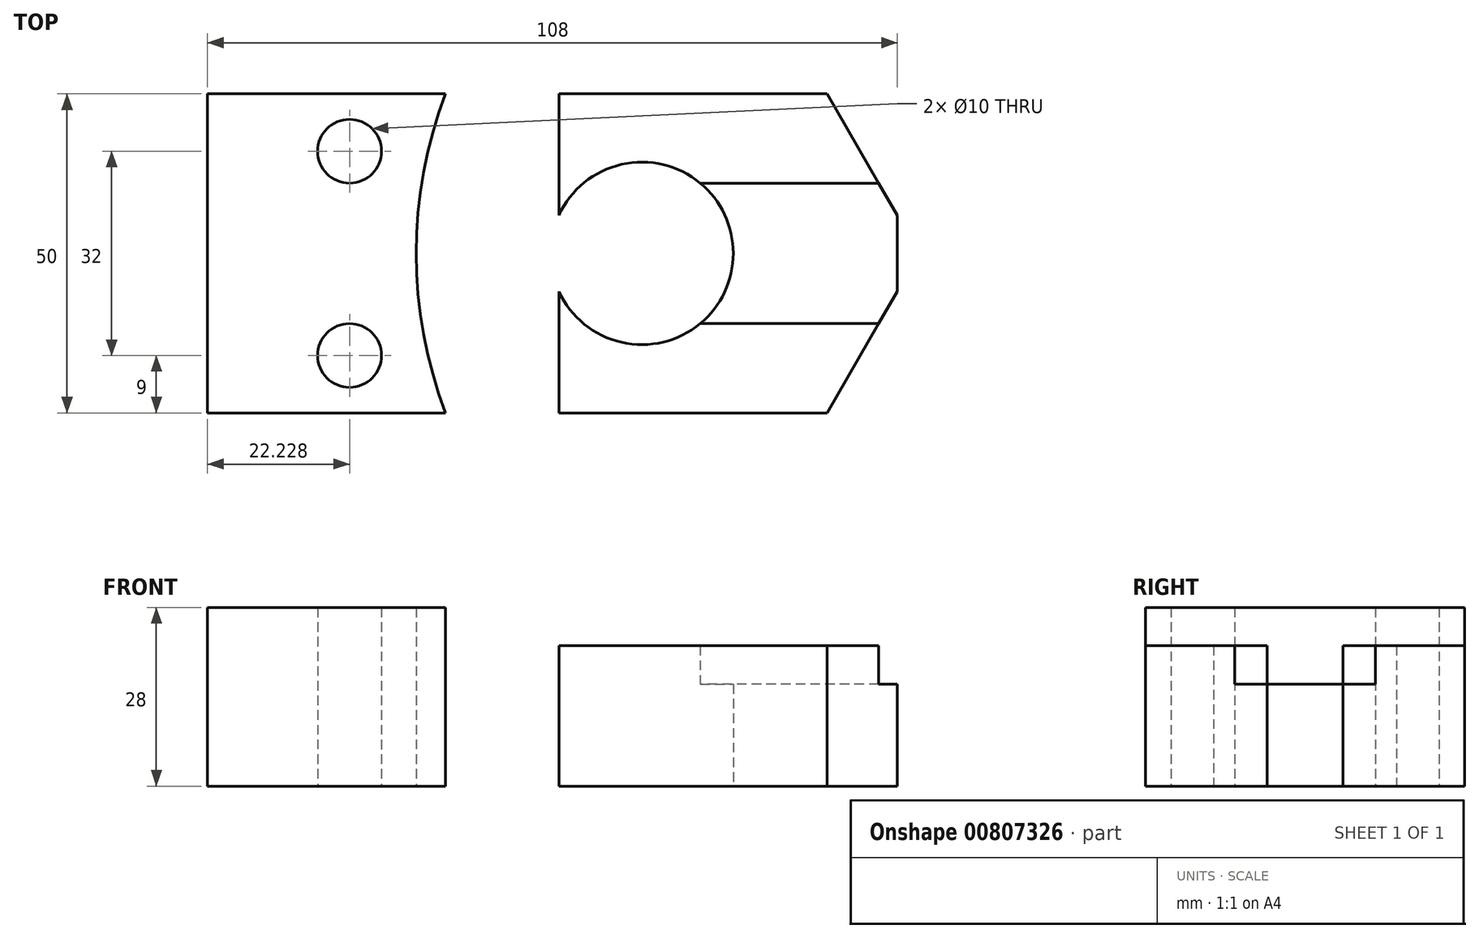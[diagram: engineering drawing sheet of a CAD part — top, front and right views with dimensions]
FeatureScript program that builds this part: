
annotation { "Feature Type Name" : "Feature", "Feature Type Description" : "" }
export const myFeature = defineFeature(function(context is Context, id is Id, definition is map)
    precondition{}
    {
        {
            var Q0;
            Q0=qCreatedBy(makeId("Top.planeOp"),FACE);
            var sketch = newSketch(context, id + "F0", { "sketchPlane" : qUnion([Q0])});
            skLineSegment(sketch, "E0", {"start": v(0, 0) * mm, "end": v(0, 50) * mm});
            skLineSegment(sketch, "E1", {"start": v(0, 50) * mm, "end": v(55, 50) * mm});
            skLineSegment(sketch, "E2", {"start": v(55, 50) * mm, "end": v(55, 0) * mm});
            skLineSegment(sketch, "E3", {"start": v(55, 0) * mm, "end": v(0, 0) * mm});
            skLineSegment(sketch, "E4", {"start": v(55, 50) * mm, "end": v(97, 50) * mm});
            skLineSegment(sketch, "E5", {"start": v(97, 50) * mm, "end": v(108, 30.95) * mm});
            skLineSegment(sketch, "E6", {"start": v(108, 30.95) * mm, "end": v(108, 19.05) * mm});
            skLineSegment(sketch, "E7", {"start": v(108, 19.05) * mm, "end": v(97, 0) * mm});
            skLineSegment(sketch, "E8", {"start": v(97, 0) * mm, "end": v(55, 0) * mm});
            skLineSegment(sketch, "E9", {"start": v(0, 25) * mm, "end": v(108, 25) * mm, "construction": true});
            skPoint(sketch, "E10", {"position": v(11, 0) * mm});
            skPoint(sketch, "E11.MirrorP", {"position": v(11, 50) * mm});
            skArc(sketch, "E12", {"start": v(11, 50) * mm, "mid": v(7.65, 25) * mm, "end": v(11, 0) * mm});
            skArc(sketch, "E13", {"start": v(37.27, 0) * mm, "mid": v(32.65, 25) * mm, "end": v(37.27, 50) * mm});
            skArc(sketch, "E14", {"start": v(24.56, 0) * mm, "mid": v(20.65, 25) * mm, "end": v(24.56, 50) * mm, "construction": true});
            skCircle(sketch, "E15", {"center": v(22.23, 41) * mm, "radius": 5 * mm});
            skCircle(sketch, "E16", {"center": v(22.23, 9) * mm, "radius": 5 * mm});
            skLineSegment(sketch, "E17", {"start": v(105.08, 14) * mm, "end": v(77.14, 14) * mm});
            skLineSegment(sketch, "E18", {"start": v(105.08, 36) * mm, "end": v(77.14, 36) * mm});
            skArc(sketch, "E19", {"start": v(77.14, 36) * mm, "mid": v(64.82, 38.94) * mm, "end": v(55, 30.96) * mm});
            skArc(sketch, "E20", {"start": v(77.14, 14) * mm, "mid": v(82.3, 25) * mm, "end": v(77.14, 36) * mm});
            skArc(sketch, "E21", {"start": v(55, 19.04) * mm, "mid": v(64.82, 11.06) * mm, "end": v(77.14, 14) * mm});
            skArc(sketch, "E22", {"start": v(55, 30.96) * mm, "mid": v(53.7, 25) * mm, "end": v(55, 19.04) * mm});
            skSolve(sketch);
        }
        {
            var Q0;
            {var subQ1=sQuery(id+"F0.wireOp",EDGE,"E12");Q0=makeQuery(id+"F0.imprint","IMPRINT",FACE,{"disambiguationData":[TD([[makeQuery(id+"F0.imprint","IMPRINT",EDGE,{"derivedFrom":subQ1}),1.0]])]});}
            extrude(context, id + "F1", {"entities" : qUnion([Q0]), "depth" : 22 * mm, "offsetDistance" : 25 * mm});
        }
        {
            var Q0;
            {var subQ0=sQuery(id+"F0.wireOp",EDGE,"E0");Q0=makeQuery(id+"F0.imprint","IMPRINT",FACE,{"disambiguationData":[TD([[makeQuery(id+"F0.imprint","IMPRINT",EDGE,{"derivedFrom":subQ0}),-1.0]])]});}
            var Q1;
            {var subQ3=sQuery(id+"F0.wireOp",EDGE,"E13");Q1=makeQuery(id+"F0.imprint","IMPRINT",FACE,{"disambiguationData":[TD([[makeQuery(id+"F0.imprint","IMPRINT",EDGE,{"derivedFrom":subQ3}),-1.0]])]});}
            extrude(context, id + "F2", {"entities" : qUnion([Q0, Q1]), "operationType" : NewBodyOperationType.ADD, "depth" : 28 * mm, "offsetDistance" : 25 * mm});
        }
        {
            var Q0;
            {var subQ2=sQuery(id+"F0.wireOp",EDGE,"E4");Q0=makeQuery(id+"F0.imprint","IMPRINT",FACE,{"disambiguationData":[TD([[makeQuery(id+"F0.imprint","IMPRINT",EDGE,{"derivedFrom":subQ2}),-1.0]])]});}
            var Q1;
            {var subQ0=sQuery(id+"F0.wireOp",EDGE,"E8");Q1=makeQuery(id+"F0.imprint","IMPRINT",FACE,{"disambiguationData":[TD([[makeQuery(id+"F0.imprint","IMPRINT",EDGE,{"derivedFrom":subQ0}),-1.0]])]});}
            extrude(context, id + "F3", {"entities" : qUnion([Q0, Q1]), "operationType" : NewBodyOperationType.ADD, "depth" : 22 * mm, "offsetDistance" : 25 * mm});
        }
        {
            var Q0;
            {var subQ2=sQuery(id+"F0.wireOp",EDGE,"E6");Q0=makeQuery(id+"F0.imprint","IMPRINT",FACE,{"disambiguationData":[TD([[makeQuery(id+"F0.imprint","IMPRINT",EDGE,{"derivedFrom":subQ2}),-1.0]])]});}
            extrude(context, id + "F4", {"entities" : qUnion([Q0]), "operationType" : NewBodyOperationType.ADD, "depth" : 16 * mm, "offsetDistance" : 25 * mm});
        }
    });
